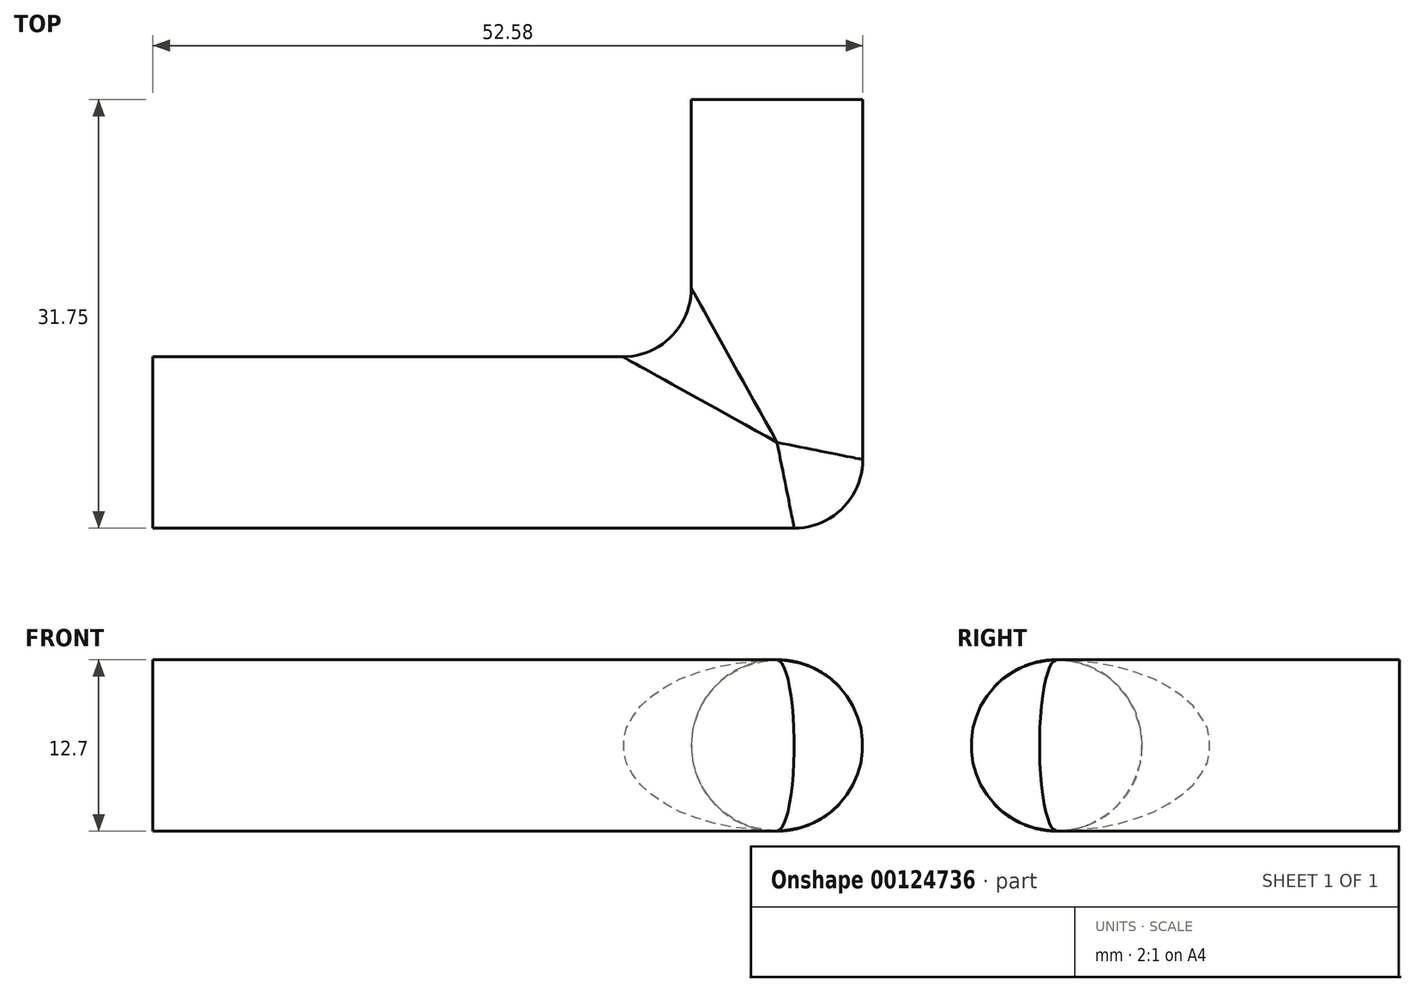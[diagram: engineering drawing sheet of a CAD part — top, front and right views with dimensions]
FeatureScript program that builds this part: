
annotation { "Feature Type Name" : "Feature", "Feature Type Description" : "" }
export const myFeature = defineFeature(function(context is Context, id is Id, definition is map)
    precondition{}
    {
        {
            var Q0;
            Q0=qCreatedBy(makeId("Front.planeOp"),FACE);
            var sketch = newSketch(context, id + "F0", { "sketchPlane" : qUnion([Q0])});
            skCircle(sketch, "E0", {"center": v(0, 0) * mm, "radius": 6.35 * mm});
            skSolve(sketch);
        }
        {
            var Q0;
            Q0=qCreatedBy(makeId("Top.planeOp"),FACE);
            var sketch = newSketch(context, id + "F1", { "sketchPlane" : qUnion([Q0])});
            skLineSegment(sketch, "E1", {"start": v(0, 0) * mm, "end": v(0, -25.4) * mm});
            skLineSegment(sketch, "E2", {"start": v(0, -25.4) * mm, "end": v(-46.23, -25.4) * mm});
            skSolve(sketch);
        }
        {
            var Q0;
            Q0=makeQuery(id+"F0.imprint","IMPRINT",FACE,{"disambiguationData":[TD([[makeQuery(id+"F0.imprint","IMPRINT",EDGE,{"derivedFrom":sQuery(id+"F0.wireOp",EDGE,"E0")}),1.0]])]});
            var Q1;
            Q1 = qConstructionFilter(qBodyType(qCreatedBy(id + "F1" ,EDGE), BodyType.WIRE), ConstructionObject.NO);
            sweep(context, id + "F2", {"profiles" : qUnion([Q0]), "path" : qUnion([Q1])});
        }
        {
            var Q0;
            Q0=makeQuery(id+"F2.opSweep","MID_CAP_EDGE",EDGE,{"disambiguationData":[OSD([sQuery(id+"F0.wireOp",EDGE,"E0"),sQuery(id+"F1.wireOp",VERTEX,"E2.start")])],"capPos":1.0});
            fillet(context, id + "F3", {"entities" : qUnion([Q0]), "radius" : 5.08 * mm, "tangentPropagation" : true, "allowEdgeOverflow" : false});
        }
    });
